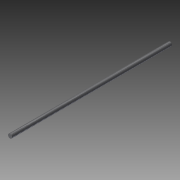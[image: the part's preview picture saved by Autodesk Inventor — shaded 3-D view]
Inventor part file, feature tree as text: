
AUTODESK INVENTOR PART (.ipt)
format: ipt  version: 2014 (Build 180170000, 170)  size: 68,096 bytes
history: native  units: mm
features: extrude x1, thread x1, sketch x1
ambient origin geometry x8: Origin, YZ Plane, XZ Plane, XY Plane, X Axis, Y Axis, Z Axis, Center Point
bodies: Solid1 (feature_tree)
feature tree (3):
  extrude  "Extrusion1"  Depth=380.0mm TaperAngle=0.0deg
  thread  "Thread2"  [1 undecoded]
  sketch  "Sketch1"  dims[d0=10.0mm d1=380.0mm d2=0.0mm d5=10.0mm d6=0.0mm]
note: 1 required parameter value undecoded (feature->parameter linkage not recoverable at this tier; creation-order binding heuristic only, values carry confidence <= 0.55)
